# Revit family: ACE-D
name_source: partatom
category: Mechanical Equipment
units: mm (PartAtom-declared; Revit-internal decimal feet)

## family parameters
Always vertical = Yes
Cut with Voids When Loaded = No
Part Type = Normal
Room Calculation Point = No
Round Connector Dimension = Use Diameter
Shared = No
Work Plane-Based = No

## types (24) — shared parameters
ONE EIGTH = 1/8"
One and a Half = 1 1/2"
Two = 2"
URL = www.lorencook.com
ZERO = 0"

## per-type parameters (varying)
| type | A_SUB | B_SUB | B_SUB_MINUS_4 | C_SUB | DEPTH | EDGE_TO_CURB | EDGE_TO_INLET | HALF_B_SUB | LOWER_WB_HEIGHT | Manufacturer | Model | RO/2 | ROOF_OPENING | T_SQ | T_SQ_HALF | Type Comments |
| 90_ACE-D | 2 1/2" | 18 3/4" | 5 3/8" | 16 13/16" | 2" | 2 1/4" | 4" | 9 3/8" | 4 1/2" | Loren Cook Company | ACED | 6 3/4" | 13 1/2" | 18" | 9" | Downblast Centrifugal Exhaust Ventilator Roof Mounted/Direct Drive |
| 70_ACE-D | 1 3/4" | 13 5/8" | 2 13/16" | 13 13/16" | 2" | 4 1/4" | 6" | 6 13/16" | 4" | Loren Cook Company
Loren Cook Company | ACED | 6 3/4" | 13 1/2" | 18" | 9" | Downblast Centrifugal Exhaust Ventilator Roof Mounted/Direct Drive |
| 100_ACE-D | 2 1/2" | 18 3/4" | 5 3/8" | 16 13/16" | 2" | 4 1/4" | 4" | 9 3/8" | 4 1/2" | Loren Cook Company | ACED | 6 3/4" | 13 1/2" | 18" | 9" | Downblast Centrifugal Exhaust Ventilator Roof Mounted/Direct Drive |
| 120_ACE-D | 1 7/16" | 28 7/16" | 10 7/32" | 27 1/16" | 2" | 4 1/4" | 3" | 14 7/32" | 7" | Loren Cook Company | ACED | 7 3/4" | 15 1/2" | 20" | 10" | Downblast Centrifugal Exhaust Ventilator Roof Mounted/Direct Drive |
| 135_ACE-D | 1 15/16" | 28 7/16" | 10 7/32" | 27 1/16" | 2" | 4 1/4" | 2 1/2" | 14 7/32" | 7" | Loren Cook Company | ACED | 7 3/4" | 15 1/2" | 20" | 10" | Downblast Centrifugal Exhaust Ventilator Roof Mounted/Direct Drive |
| 150_ACE-D | 2 13/16" | 32 7/8" | 12 7/16" | 28 11/16" | 2" | 4 1/4" | 3" | 16 7/16" | 7" | Loren Cook Company | ACED | 9 3/4" | 19 1/2" | 24" | 12" | Downblast Centrifugal Exhaust Ventilator Roof Mounted/Direct Drive |
| 165_ACE-D | 3 5/16" | 32 7/8" | 12 7/16" | 29 3/16" | 2" | 4 1/4" | 3" | 16 7/16" | 7" | Loren Cook Company | ACED | 9 3/4" | 19 1/2" | 24" | 12" | Downblast Centrifugal Exhaust Ventilator Roof Mounted/Direct Drive |
| 180_ACE-D | 3 5/16" | 37 11/16" | 14 27/32" | 33 15/16" | 3" | 4 1/4" | 3 3/4" | 18 27/32" | 6 5/16" | Loren Cook Company | ACED | 12 3/4" | 25 1/2" | 30" | 15" | Downblast Centrifugal Exhaust Ventilator Roof Mounted/Direct Drive |
| 195_ACE-D | 4 7/16" | 37 11/16" | 14 27/32" | 35" | 3" | 4 1/4" | 3 3/4" | 18 27/32" | 6 5/16" | Loren Cook Company | ACED | 12 3/4" | 25 1/2" | 30" | 15" | Downblast Centrifugal Exhaust Ventilator Roof Mounted/Direct Drive |
| 210_ACE-D | 4 3/4" | 43 5/8" | 17 13/16" | 37 1/4" | 3" | 4 1/4" | 3 3/4" | 21 13/16" | 6 5/16" | Loren Cook Company | ACED | 12 3/4" | 25 1/2" | 30" | 15" | Downblast Centrifugal Exhaust Ventilator Roof Mounted/Direct Drive |
| 225_ACE-D | 4 7/8" | 43 5/8" | 17 13/16" | 37 3/8" | 3" | 4 1/4" | 3 3/4" | 21 13/16" | 6 5/16" | Loren Cook Company | ACED | 12 3/4" | 25 1/2" | 30" | 15" | Downblast Centrifugal Exhaust Ventilator Roof Mounted/Direct Drive |
| 245_ACE-D | 6 1/8" | 47 5/8" | 19 13/16" | 39 7/8" | 3" | 4 1/4" | 3 3/4" | 23 13/16" | 6 5/16" | Loren Cook Company | ACED | 12 3/4" | 25 1/2" | 30" | 15" | Downblast Centrifugal Exhaust Ventilator Roof Mounted/Direct Drive |
| 270_ACE-D | 6 1/8" | 47 5/8" | 19 13/16" | 39 7/8" | 3" | 4 1/4" | 3 3/4" | 23 13/16" | 6 5/16" | Loren Cook Company | ACED | 15 3/4" | 31 1/2" | 36" | 18" | Downblast Centrifugal Exhaust Ventilator Roof Mounted/Direct Drive |
| 300_ACE-D | 7 1/16" | 52 5/8" | 22 5/16" | 49 1/16" | 3" | 4 1/4" | 3 3/4" | 26 5/16" | 6 5/16" | Loren Cook Company | ACED | 15 3/4" | 31 1/2" | 36" | 18" | Downblast Centrifugal Exhaust Ventilator Roof Mounted/Direct Drive |
| 100_ACE-VF | 2 1/2" | 18 3/4" | 5 3/8" | 16 13/16" | 2" | 4 1/4" | 4" | 9 3/8" | 4 1/2" | Loren Cook Company | ACED VF | 6 3/4" | 13 1/2" | 18" | 9" | Downblast Centrifugal Exhaust Ventilator Roof Mounted/Direct Drive Electronically Commutated Vari-Flow Motor |
| 120_ACE-VF | 1 7/16" | 28 7/16" | 10 7/32" | 27 1/16" | 2" | 4 1/4" | 3" | 14 7/32" | 7" | Loren Cook Company | ACED VF | 7 3/4" | 15 1/2" | 20" | 10" | Downblast Centrifugal Exhaust Ventilator Roof Mounted/Direct Drive Electronically Commutated Vari-Flow Motor |
| 135_ACE-VF | 1 15/16" | 28 7/16" | 10 7/32" | 27 1/16" | 2" | 4 1/4" | 2 1/2" | 14 7/32" | 7" | Loren Cook Company | ACED VF | 7 3/4" | 15 1/2" | 20" | 10" | Downblast Centrifugal Exhaust Ventilator Roof Mounted/Direct Drive Electronically Commutated Vari-Flow Motor |
| 150_ACE-VF | 2 13/16" | 32 7/8" | 12 7/16" | 28 11/16" | 2" | 4 1/4" | 3" | 16 7/16" | 7" | Loren Cook Company | ACED VF | 9 3/4" | 19 1/2" | 24" | 12" | Downblast Centrifugal Exhaust Ventilator Roof Mounted/Direct Drive Electronically Commutated Vari-Flow Motor |
| 165_ACE-VF | 3 5/16" | 32 7/8" | 12 7/16" | 29 3/16" | 2" | 4 1/4" | 3" | 16 7/16" | 7" | Loren Cook Company | ACED VF | 9 3/4" | 19 1/2" | 24" | 12" | Downblast Centrifugal Exhaust Ventilator Roof Mounted/Direct Drive Electronically Commutated Vari-Flow Motor |
| 180_ACE-VF | 3 5/16" | 37 11/16" | 14 27/32" | 33 15/16" | 3" | 4 1/4" | 3 3/4" | 18 27/32" | 6 5/16" | Loren Cook Company | ACED VF | 12 3/4" | 25 1/2" | 30" | 15" | Downblast Centrifugal Exhaust Ventilator Roof Mounted/Direct Drive Electronically Commutated Vari-Flow Motor |
| 195_ACE-VF | 4 7/16" | 37 11/16" | 14 27/32" | 35" | 3" | 4 1/4" | 3 3/4" | 18 27/32" | 6 5/16" | Loren Cook Company | ACED VF | 12 3/4" | 25 1/2" | 30" | 15" | Downblast Centrifugal Exhaust Ventilator Roof Mounted/Direct Drive Electronically Commutated Vari-Flow Motor |
| 210_ACE-VF | 4 3/4" | 43 5/8" | 17 13/16" | 37 1/4" | 3" | 4 1/4" | 3 3/4" | 21 13/16" | 6 5/16" | Loren Cook Company | ACED VF | 12 3/4" | 25 1/2" | 30" | 15" | Downblast Centrifugal Exhaust Ventilator Roof Mounted/Direct Drive Electronically Commutated Vari-Flow Motor |
| 101_ACE-D | 2 3/8" | 23 9/16" | 7 25/32" | 21 1/8" | 2" | 4 1/4" | 4" | 11 25/32" | 4 1/2" | Loren Cook Company | ACED | 6 3/4" | 13 1/2" | 18" | 9" | Downblast Centrifugal Exhaust Ventilator Roof Mounted/Direct Drive |
| 101_ACE-VF | 2 3/8" | 23 9/16" | 7 25/32" | 21 1/8" | 2" | 4 1/4" | 4" | 11 25/32" | 4 1/2" | Loren Cook Company | ACED | 6 3/4" | 13 1/2" | 18" | 9" | Downblast Centrifugal Exhaust Ventilator Roof Mounted/Direct Drive |

## geometry (parser evidence)
native form markers: Sweep x3
no freeform markers — native parametric forms only
